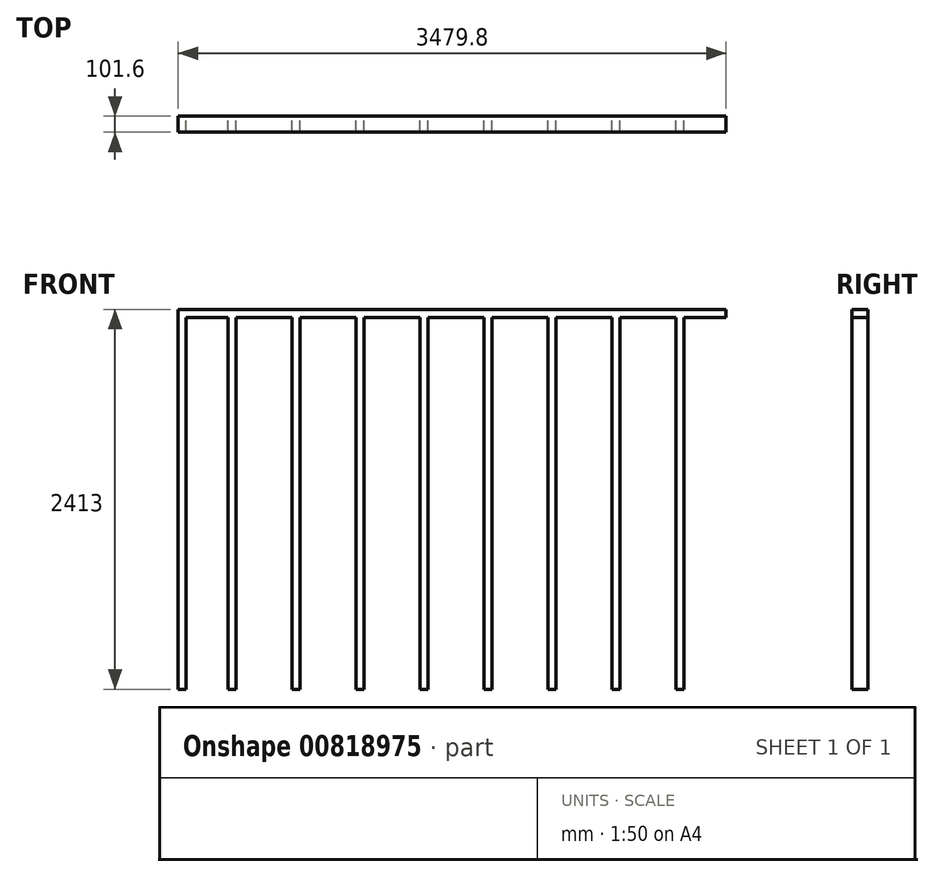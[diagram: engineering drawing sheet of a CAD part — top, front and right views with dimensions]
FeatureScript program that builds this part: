
annotation { "Feature Type Name" : "Feature", "Feature Type Description" : "" }
export const myFeature = defineFeature(function(context is Context, id is Id, definition is map)
    precondition{}
    {
        {
            var Q0;
            Q0=qCreatedBy(makeId("Front.planeOp"),FACE);
            var sketch = newSketch(context, id + "F0", { "sketchPlane" : qUnion([Q0])});
            skLineSegment(sketch, "E0", {"start": v(-77.02, 1950.4) * mm, "end": v(-77.02, -411.8) * mm});
            skLineSegment(sketch, "E1", {"start": v(-77.02, -411.8) * mm, "end": v(-26.22, -411.8) * mm});
            skLineSegment(sketch, "E2", {"start": v(-26.22, -411.8) * mm, "end": v(-26.22, 1950.4) * mm});
            skLineSegment(sketch, "E3", {"start": v(-77.02, 1950.4) * mm, "end": v(-26.22, 1950.4) * mm});
            skSolve(sketch);
        }
        {
            var Q0;
            Q0=makeQuery(id+"F0.imprint","IMPRINT",FACE,{"disambiguationData":[TD([[makeQuery(id+"F0.imprint","IMPRINT",EDGE,{"derivedFrom":sQuery(id+"F0.wireOp",EDGE,"E0")}),1.0]])]});
            extrude(context, id + "F1", {"entities" : qUnion([Q0]), "depth" : 101.6 * mm, "offsetDistance" : 25.4 * mm});
        }
        {
            var Q0;
            Q0=makeQuery(id+"F1.opExtrude","SWEPT_FACE",FACE,{"disambiguationData":[OSD([sQuery(id+"F0.wireOp",EDGE,"E0")])]});
            var sketch = newSketch(context, id + "F2", { "sketchPlane" : qUnion([Q0])});
            skLineSegment(sketch, "E4", {"start": v(0, 1950.4) * mm, "end": v(101.6, 1950.4) * mm});
            skLineSegment(sketch, "E5", {"start": v(101.6, 1950.4) * mm, "end": v(101.6, 2001.2) * mm});
            skLineSegment(sketch, "E6", {"start": v(101.6, 2001.2) * mm, "end": v(0, 2001.2) * mm});
            skLineSegment(sketch, "E7", {"start": v(0, 2001.2) * mm, "end": v(0, 1950.4) * mm});
            skSolve(sketch);
        }
        {
            var Q0;
            Q0=makeQuery(id+"F2.imprint","IMPRINT",FACE,{"disambiguationData":[TD([[makeQuery(id+"F2.imprint","IMPRINT",EDGE,{"derivedFrom":sQuery(id+"F2.wireOp",EDGE,"E4")}),-1.0]])]});
            extrude(context, id + "F3", {"entities" : qUnion([Q0]), "operationType" : NewBodyOperationType.ADD, "oppositeDirection" : true, "depth" : 3479.8 * mm, "offsetDistance" : 25.4 * mm});
        }
        {
            var Q0;
            Q0=makeQuery(id+"F3.opExtrude","SWEPT_FACE",FACE,{"disambiguationData":[OSD([sQuery(id+"F2.wireOp",EDGE,"E4")])]});
            var sketch = newSketch(context, id + "F4", { "sketchPlane" : qUnion([Q0])});
            skLineSegment(sketch, "E8.bottom", {"start": v(240.48, 101.6) * mm, "end": v(291.28, 101.6) * mm});
            skLineSegment(sketch, "E8.top", {"start": v(240.48, 0) * mm, "end": v(291.28, 0) * mm});
            skLineSegment(sketch, "E8.left", {"start": v(240.48, 101.6) * mm, "end": v(240.48, 0) * mm});
            skLineSegment(sketch, "E8.right", {"start": v(291.28, 101.6) * mm, "end": v(291.28, 0) * mm});
            skLineSegment(sketch, "E9.1.0.0", {"start": v(646.88, 101.6) * mm, "end": v(646.88, 0) * mm});
            skLineSegment(sketch, "E9.1.0.1", {"start": v(646.88, 101.6) * mm, "end": v(697.68, 101.6) * mm});
            skLineSegment(sketch, "E9.1.0.2", {"start": v(697.68, 101.6) * mm, "end": v(697.68, 0) * mm});
            skLineSegment(sketch, "E9.1.0.3", {"start": v(646.88, 0) * mm, "end": v(697.68, 0) * mm});
            skLineSegment(sketch, "E9.2.0.0", {"start": v(1053.28, 101.6) * mm, "end": v(1053.28, 0) * mm});
            skLineSegment(sketch, "E9.2.0.1", {"start": v(1053.28, 101.6) * mm, "end": v(1104.08, 101.6) * mm});
            skLineSegment(sketch, "E9.2.0.2", {"start": v(1104.08, 101.6) * mm, "end": v(1104.08, 0) * mm});
            skLineSegment(sketch, "E9.2.0.3", {"start": v(1053.28, 0) * mm, "end": v(1104.08, 0) * mm});
            skLineSegment(sketch, "E9.3.0.0", {"start": v(1459.68, 101.6) * mm, "end": v(1459.68, 0) * mm});
            skLineSegment(sketch, "E9.3.0.1", {"start": v(1459.68, 101.6) * mm, "end": v(1510.48, 101.6) * mm});
            skLineSegment(sketch, "E9.3.0.2", {"start": v(1510.48, 101.6) * mm, "end": v(1510.48, 0) * mm});
            skLineSegment(sketch, "E9.3.0.3", {"start": v(1459.68, 0) * mm, "end": v(1510.48, 0) * mm});
            skLineSegment(sketch, "E9.direction1", {"start": v(240.48, 0) * mm, "end": v(646.88, 0) * mm, "construction": true});
            skLineSegment(sketch, "E10.0.4.0", {"start": v(1866.08, 101.6) * mm, "end": v(1866.08, 0) * mm});
            skLineSegment(sketch, "E10.3.4.0", {"start": v(1866.08, 101.6) * mm, "end": v(1916.88, 101.6) * mm});
            skLineSegment(sketch, "E10.6.4.0", {"start": v(1916.88, 101.6) * mm, "end": v(1916.88, 0) * mm});
            skLineSegment(sketch, "E10.9.4.0", {"start": v(1866.08, 0) * mm, "end": v(1916.88, 0) * mm});
            skLineSegment(sketch, "E11.0.5.0", {"start": v(2272.48, 101.6) * mm, "end": v(2272.48, 0) * mm});
            skLineSegment(sketch, "E11.3.5.0", {"start": v(2272.48, 101.6) * mm, "end": v(2323.28, 101.6) * mm});
            skLineSegment(sketch, "E11.6.5.0", {"start": v(2323.28, 101.6) * mm, "end": v(2323.28, 0) * mm});
            skLineSegment(sketch, "E11.9.5.0", {"start": v(2272.48, 0) * mm, "end": v(2323.28, 0) * mm});
            skLineSegment(sketch, "E12.0.6.0", {"start": v(2678.88, 101.6) * mm, "end": v(2678.88, 0) * mm});
            skLineSegment(sketch, "E12.3.6.0", {"start": v(2678.88, 101.6) * mm, "end": v(2729.68, 101.6) * mm});
            skLineSegment(sketch, "E12.6.6.0", {"start": v(2729.68, 101.6) * mm, "end": v(2729.68, 0) * mm});
            skLineSegment(sketch, "E12.9.6.0", {"start": v(2678.88, 0) * mm, "end": v(2729.68, 0) * mm});
            skLineSegment(sketch, "E12.0.7.0", {"start": v(3085.28, 101.6) * mm, "end": v(3085.28, 0) * mm});
            skLineSegment(sketch, "E12.3.7.0", {"start": v(3085.28, 101.6) * mm, "end": v(3136.08, 101.6) * mm});
            skLineSegment(sketch, "E12.6.7.0", {"start": v(3136.08, 101.6) * mm, "end": v(3136.08, 0) * mm});
            skLineSegment(sketch, "E12.9.7.0", {"start": v(3085.28, 0) * mm, "end": v(3136.08, 0) * mm});
            skSolve(sketch);
        }
        {
            var Q0;
            Q0=makeQuery(id+"F4.imprint","IMPRINT",FACE,{"disambiguationData":[TD([[makeQuery(id+"F4.imprint","IMPRINT",EDGE,{"derivedFrom":sQuery(id+"F4.wireOp",EDGE,"E8.bottom")}),1.0]])]});
            var Q1;
            Q1=makeQuery(id+"F4.imprint","IMPRINT",FACE,{"disambiguationData":[TD([[makeQuery(id+"F4.imprint","IMPRINT",EDGE,{"derivedFrom":sQuery(id+"F4.wireOp",EDGE,"E9.1.0.0")}),1.0]])]});
            var Q2;
            Q2=makeQuery(id+"F4.imprint","IMPRINT",FACE,{"disambiguationData":[TD([[makeQuery(id+"F4.imprint","IMPRINT",EDGE,{"derivedFrom":sQuery(id+"F4.wireOp",EDGE,"E9.2.0.0")}),1.0]])]});
            var Q3;
            Q3=makeQuery(id+"F4.imprint","IMPRINT",FACE,{"disambiguationData":[TD([[makeQuery(id+"F4.imprint","IMPRINT",EDGE,{"derivedFrom":sQuery(id+"F4.wireOp",EDGE,"E9.3.0.0")}),1.0]])]});
            var Q4;
            Q4=makeQuery(id+"F4.imprint","IMPRINT",FACE,{"disambiguationData":[TD([[makeQuery(id+"F4.imprint","IMPRINT",EDGE,{"derivedFrom":sQuery(id+"F4.wireOp",EDGE,"E10.0.4.0")}),1.0]])]});
            var Q5;
            Q5=makeQuery(id+"F4.imprint","IMPRINT",FACE,{"disambiguationData":[TD([[makeQuery(id+"F4.imprint","IMPRINT",EDGE,{"derivedFrom":sQuery(id+"F4.wireOp",EDGE,"E11.0.5.0")}),1.0]])]});
            var Q6;
            Q6=makeQuery(id+"F4.imprint","IMPRINT",FACE,{"disambiguationData":[TD([[makeQuery(id+"F4.imprint","IMPRINT",EDGE,{"derivedFrom":sQuery(id+"F4.wireOp",EDGE,"E12.0.6.0")}),1.0]])]});
            var Q7;
            Q7=makeQuery(id+"F4.imprint","IMPRINT",FACE,{"disambiguationData":[TD([[makeQuery(id+"F4.imprint","IMPRINT",EDGE,{"derivedFrom":sQuery(id+"F4.wireOp",EDGE,"E12.0.7.0")}),1.0]])]});
            var Q8;
            Q8=makeQuery(id+"F4.imprint","IMPRINT",FACE,{"disambiguationData":[TD([[makeQuery(id+"F4.imprint","IMPRINT",EDGE,{"derivedFrom":sQuery(id+"F4.wireOp",EDGE,"E12.0.8.0")}),1.0]])]});
            extrude(context, id + "F5", {"entities" : qUnion([Q0, Q1, Q2, Q3, Q4, Q5, Q6, Q7, Q8]), "operationType" : NewBodyOperationType.ADD, "depth" : 2362.2 * mm, "offsetDistance" : 25.4 * mm});
        }
    });
